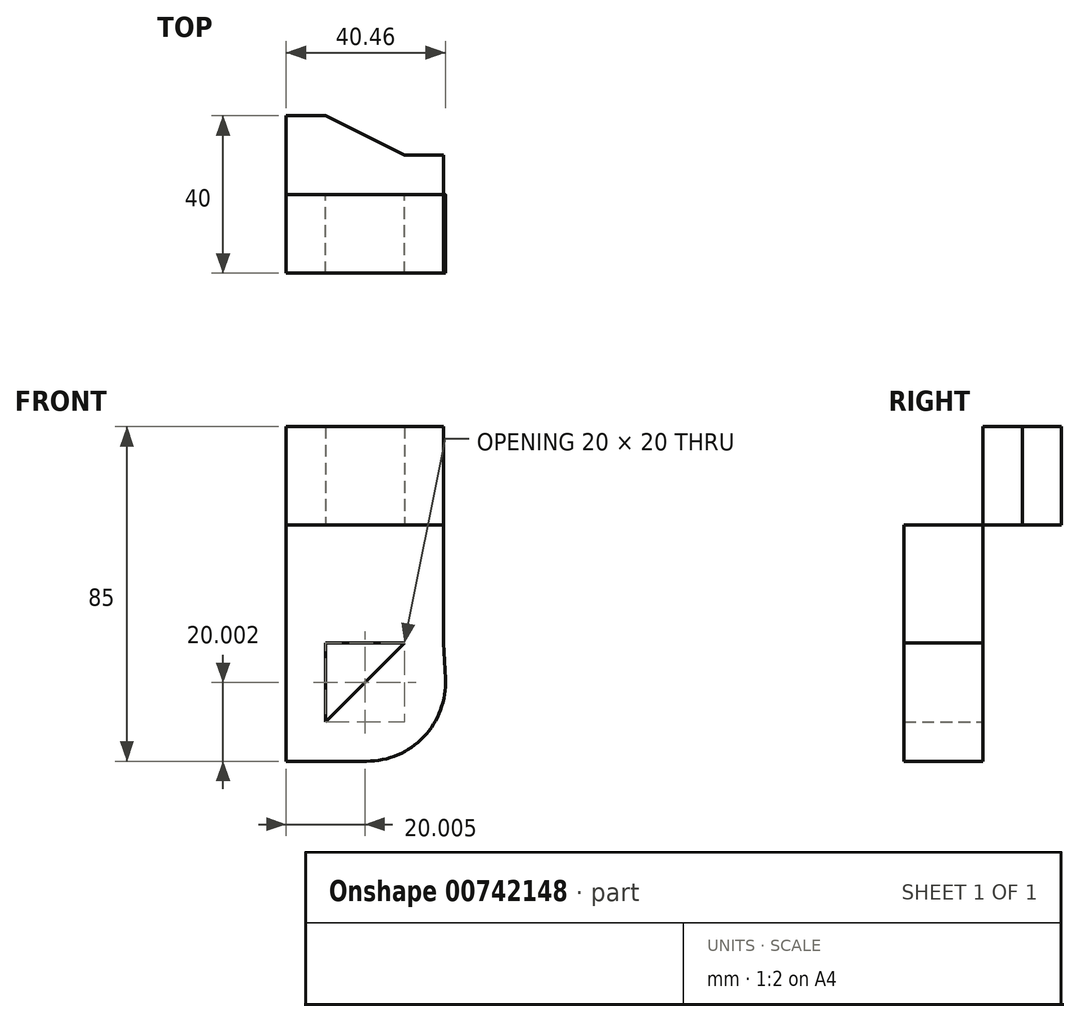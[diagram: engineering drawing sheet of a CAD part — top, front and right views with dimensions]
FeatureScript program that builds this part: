
annotation { "Feature Type Name" : "Feature", "Feature Type Description" : "" }
export const myFeature = defineFeature(function(context is Context, id is Id, definition is map)
    precondition{}
    {
        {
            var Q0;
            Q0=qCreatedBy(makeId("Front.planeOp"),FACE);
            var sketch = newSketch(context, id + "F0", { "sketchPlane" : qUnion([Q0])});
            skLineSegment(sketch, "E0", {"start": v(-21.59, 68.92) * mm, "end": v(-21.59, 38.92) * mm});
            skLineSegment(sketch, "E1", {"start": v(-21.59, 38.92) * mm, "end": v(-21.59, 18.92) * mm});
            skLineSegment(sketch, "E2", {"start": v(-21.59, 18.92) * mm, "end": v(-21.59, 8.92) * mm});
            skLineSegment(sketch, "E3", {"start": v(-21.59, 8.92) * mm, "end": v(-11.59, 8.92) * mm});
            skLineSegment(sketch, "E4", {"start": v(-21.59, 68.92) * mm, "end": v(18.41, 68.92) * mm});
            skLineSegment(sketch, "E5", {"start": v(18.41, 68.92) * mm, "end": v(18.41, 48.92) * mm});
            skLineSegment(sketch, "E6", {"start": v(18.41, 48.92) * mm, "end": v(18.41, 38.92) * mm});
            skLineSegment(sketch, "E7", {"start": v(-11.59, 8.92) * mm, "end": v(-1.13, 8.92) * mm});
            skLineSegment(sketch, "E8", {"start": v(18.41, 38.92) * mm, "end": v(18.85, 29.88) * mm});
            skPoint(sketch, "E9.visualSharp", {"position": v(19.86, 8.92) * mm});
            skArc(sketch, "E9.filletArc", {"start": v(-1.13, 8.92) * mm, "mid": v(13.35, 15.12) * mm, "end": v(18.85, 29.88) * mm});
            skLineSegment(sketch, "E10", {"start": v(-11.59, 18.92) * mm, "end": v(-11.59, 38.92) * mm});
            skLineSegment(sketch, "E11", {"start": v(-11.59, 38.92) * mm, "end": v(8.41, 38.92) * mm});
            skLineSegment(sketch, "E12", {"start": v(-11.59, 18.92) * mm, "end": v(8.41, 38.92) * mm});
            skLineSegment(sketch, "E13", {"start": v(18.41, 48.92) * mm, "end": v(-21.59, 48.92) * mm});
            skLineSegment(sketch, "E14", {"start": v(-11.59, 68.92) * mm, "end": v(-11.59, 48.92) * mm});
            skLineSegment(sketch, "E15", {"start": v(8.92, 68.92) * mm, "end": v(8.92, 48.92) * mm});
            skSolve(sketch);
        }
        {
            var Q0;
            Q0 = qSketchRegion(id + "F0", true);
            extrude(context, id + "F1", {"entities" : qUnion([Q0]), "depth" : 20 * mm, "offsetDistance" : 25 * mm});
        }
        {
            var Q0;
            Q0=makeQuery(id+"F1.opExtrude","SWEPT_FACE",FACE,{"disambiguationData":[OSD([sQuery(id+"F0.wireOp",EDGE,"E4")])]});
            var sketch = newSketch(context, id + "F2", { "sketchPlane" : qUnion([Q0])});
            skLineSegment(sketch, "E16", {"start": v(-21.59, 0) * mm, "end": v(-21.59, 20) * mm});
            skLineSegment(sketch, "E17", {"start": v(-21.59, 20) * mm, "end": v(-11.59, 20) * mm});
            skLineSegment(sketch, "E18", {"start": v(18.41, 0) * mm, "end": v(18.41, 10) * mm});
            skLineSegment(sketch, "E19", {"start": v(18.41, 10) * mm, "end": v(8.41, 10) * mm});
            skLineSegment(sketch, "E20", {"start": v(-11.59, 20) * mm, "end": v(8.41, 10) * mm});
            skSolve(sketch);
        }
        {
            var Q0;
            Q0 = qSketchRegion(id + "F2", true);
            var Q1;
            Q1=makeQuery(id+"F2.imprint","IMPRINT",FACE,{"disambiguationData":[TD([[makeQuery(id+"F2.imprint","IMPRINT",EDGE,{"derivedFrom":sQuery(id+"F2.wireOp",EDGE,"E16")}),-1.0]])]});
            extrude(context, id + "F3", {"entities" : qUnion([Q0, Q1]), "depth" : 25 * mm, "offsetDistance" : 25 * mm});
        }
    });
